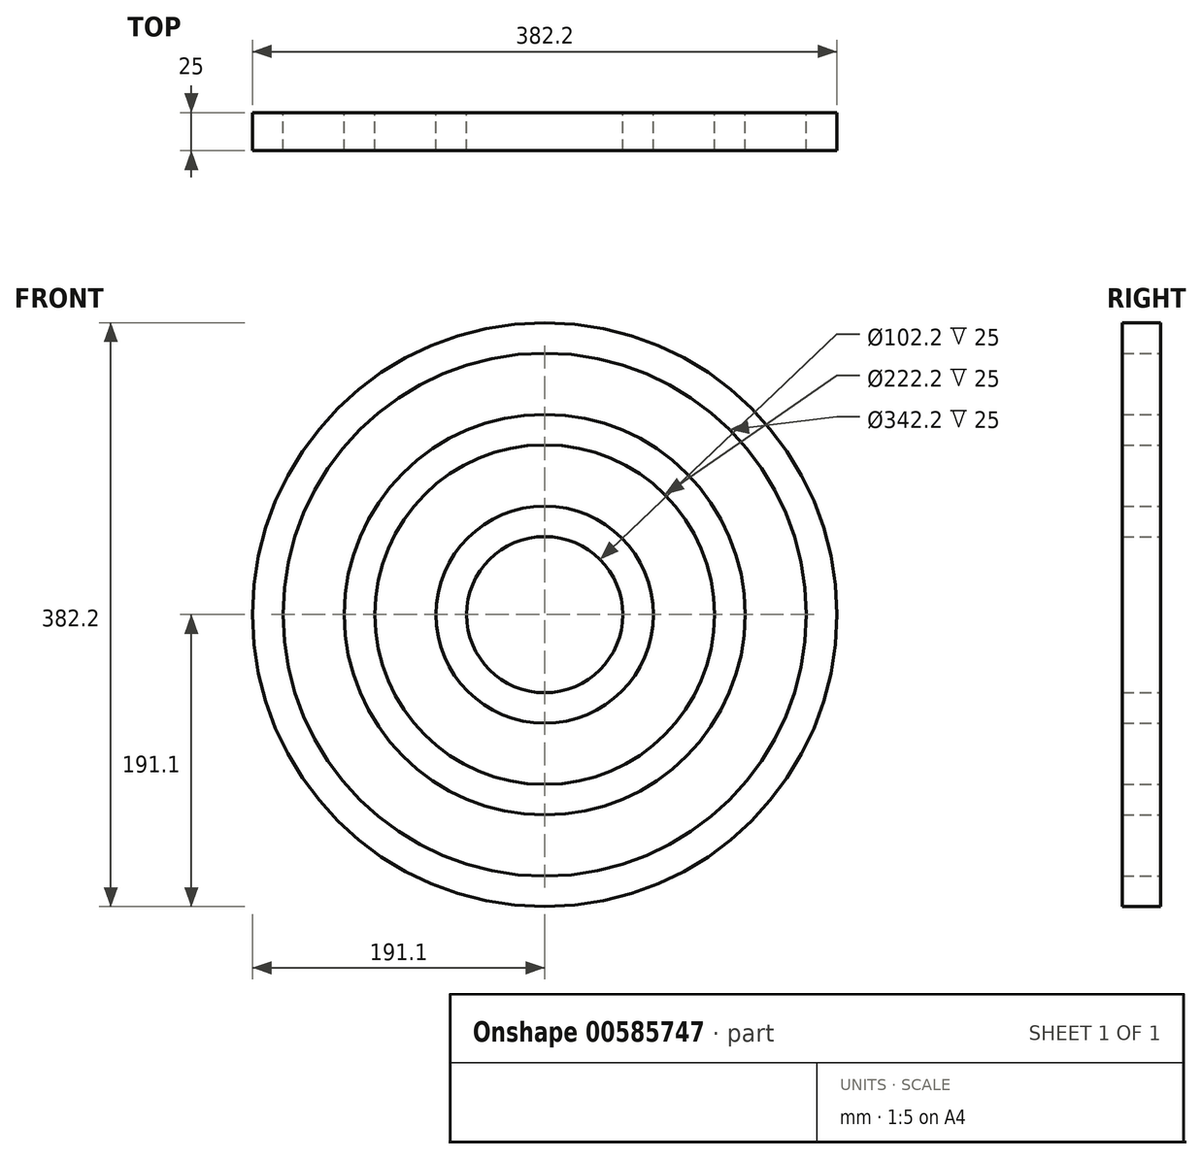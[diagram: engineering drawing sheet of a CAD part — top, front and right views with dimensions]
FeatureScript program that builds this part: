
annotation { "Feature Type Name" : "Feature", "Feature Type Description" : "" }
export const myFeature = defineFeature(function(context is Context, id is Id, definition is map)
    precondition{}
    {
        {
            var Q0;
            Q0=qCreatedBy(makeId("Front.planeOp"),FACE);
            var sketch = newSketch(context, id + "F0", { "sketchPlane" : qUnion([Q0])});
            skPoint(sketch, "E0", {"position": v(0, 0) * mm});
            skCircle(sketch, "E1", {"center": v(0, 0) * mm, "radius": 51.1 * mm});
            skCircle(sketch, "E2.0", {"center": v(0, 0) * mm, "radius": 71.1 * mm});
            skCircle(sketch, "E3.0", {"center": v(0, 0) * mm, "radius": 31.1 * mm});
            skCircle(sketch, "E4.0", {"center": v(0, 0) * mm, "radius": 91.1 * mm});
            skCircle(sketch, "E5.0", {"center": v(0, 0) * mm, "radius": 111.1 * mm});
            skCircle(sketch, "E6.0", {"center": v(0, 0) * mm, "radius": 131.1 * mm});
            skCircle(sketch, "E7.0", {"center": v(0, 0) * mm, "radius": 11.1 * mm});
            skCircle(sketch, "E8.0", {"center": v(0, 0) * mm, "radius": 151.1 * mm});
            skCircle(sketch, "E9.0", {"center": v(0, 0) * mm, "radius": 171.1 * mm});
            skCircle(sketch, "E10.0", {"center": v(0, 0) * mm, "radius": 191.1 * mm});
            skSolve(sketch);
        }
        {
            var Q0;
            Q0=makeQuery(id+"F0.imprint","IMPRINT",FACE,{"disambiguationData":[TD([[makeQuery(id+"F0.imprint","IMPRINT",EDGE,{"derivedFrom":sQuery(id+"F0.wireOp",EDGE,"E9.0")}),-1.0]])]});
            var Q1;
            Q1=makeQuery(id+"F0.imprint","IMPRINT",FACE,{"disambiguationData":[TD([[makeQuery(id+"F0.imprint","IMPRINT",EDGE,{"derivedFrom":sQuery(id+"F0.wireOp",EDGE,"E1")}),-1.0]])]});
            var Q2;
            Q2=makeQuery(id+"F0.imprint","IMPRINT",FACE,{"disambiguationData":[TD([[makeQuery(id+"F0.imprint","IMPRINT",EDGE,{"derivedFrom":sQuery(id+"F0.wireOp",EDGE,"E5.0")}),-1.0]])]});
            extrude(context, id + "F1", {"entities" : qUnion([Q0, Q1, Q2]), "depth" : 25 * mm, "offsetDistance" : 25 * mm});
        }
    });
